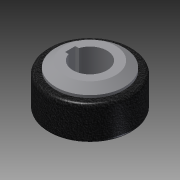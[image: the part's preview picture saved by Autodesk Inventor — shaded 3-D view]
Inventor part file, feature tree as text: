
AUTODESK INVENTOR PART (.ipt)
format: ipt  version: 2015 (Build 190159000, 159)  size: 150,528 bytes
history: native  units: mm
features: extrude x4, sketch x4, chamfer x2, fillet x1
ambient origin geometry x8: Origin, YZ Plane, XZ Plane, XY Plane, X Axis, Y Axis, Z Axis, Center Point
bodies: 实体1 (feature_tree)
feature tree (11):
  extrude  "拉伸1"  Depth=20.0mm TaperAngle=0.0deg
  extrude  "拉伸2"  Depth=5.0mm TaperAngle=0.0deg
  chamfer  "倒角1"  Distance=5.0mm Angle=45.0deg
  extrude  "拉伸3"  Depth=5.0mm TaperAngle=0.0deg
  chamfer  "倒角2"  Distance=5.0mm Angle=45.0deg
  fillet  "圆角1"  Radius=2.0mm
  extrude  "拉伸4"  Depth=6.0mm
  sketch  "草图1"  dims[d0=49.0mm d1=20.0mm d2=0.0mm]
  sketch  "草图2"  dims[d3=40.0mm d4=5.0mm d5=0.0mm d6=5.0mm d7=3.5mm d8=45.0deg]
  sketch  "草图3"  dims[d9=40.0mm d10=5.0mm d11=0.0mm d12=5.0mm d13=3.5mm d14=45.0deg d15=2.0mm]
  sketch  "草图4"  dims[d16=20.0mm d17=6.0mm d18=11.6mm d19=5.0mm d20=0.0mm]
